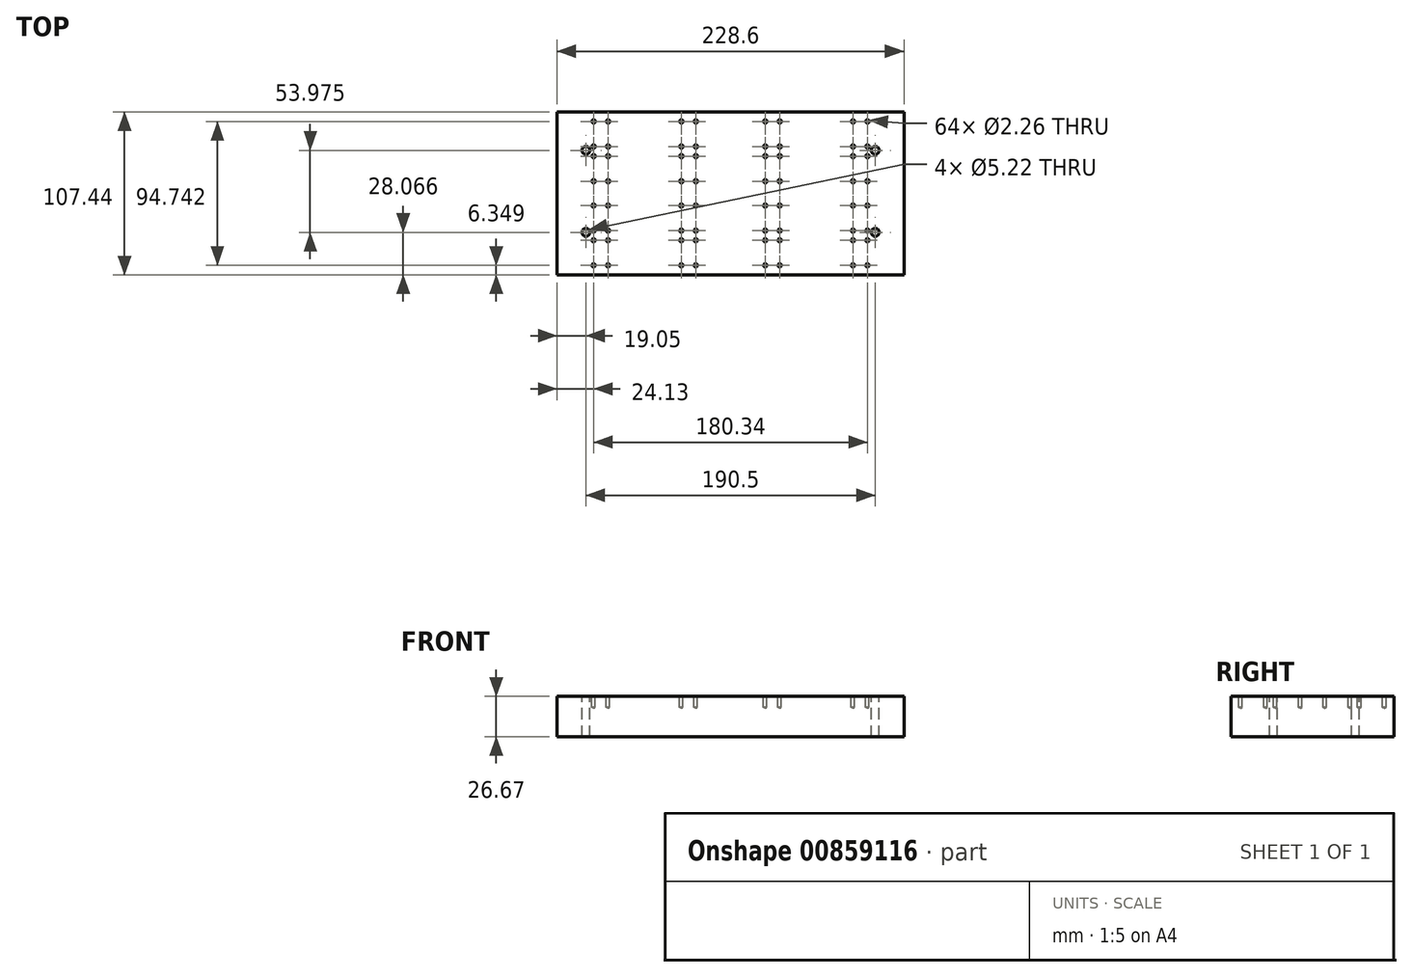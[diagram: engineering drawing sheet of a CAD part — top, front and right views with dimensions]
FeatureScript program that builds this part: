
annotation { "Feature Type Name" : "Feature", "Feature Type Description" : "" }
export const myFeature = defineFeature(function(context is Context, id is Id, definition is map)
    precondition{}
    {
        {
            var Q0;
            Q0=qCreatedBy(makeId("Top.planeOp"),FACE);
            var sketch = newSketch(context, id + "F0", { "sketchPlane" : qUnion([Q0])});
            skLineSegment(sketch, "E0.bottom", {"start": v(-114.3, 53.72) * mm, "end": v(114.3, 53.72) * mm});
            skLineSegment(sketch, "E0.top", {"start": v(-114.3, -53.72) * mm, "end": v(114.3, -53.72) * mm});
            skLineSegment(sketch, "E0.left", {"start": v(-114.3, 53.72) * mm, "end": v(-114.3, -53.72) * mm});
            skLineSegment(sketch, "E0.right", {"start": v(114.3, 53.72) * mm, "end": v(114.3, -53.72) * mm});
            skPoint(sketch, "E0.middle", {"position": v(0, 0) * mm});
            skSolve(sketch);
        }
        {
            var Q0;
            Q0=makeQuery(id+"F0.imprint","IMPRINT",FACE,{"disambiguationData":[TD([[makeQuery(id+"F0.imprint","IMPRINT",EDGE,{"derivedFrom":sQuery(id+"F0.wireOp",EDGE,"E0.bottom")}),-1.0]])]});
            extrude(context, id + "F1", {"entities" : qUnion([Q0]), "depth" : 26.67 * mm, "offsetDistance" : 25.4 * mm});
        }
        {
            var Q0;
            Q0=makeQuery(id+"F1.opExtrude","CAP_FACE",FACE,{"disambiguationData":[OSD([sQuery(id+"F0.wireOp",EDGE,"E0.bottom"),sQuery(id+"F0.wireOp",EDGE,"E0.top"),sQuery(id+"F0.wireOp",EDGE,"E0.left"),sQuery(id+"F0.wireOp",EDGE,"E0.right")])],"isStart":false});
            var sketch = newSketch(context, id + "F2", { "sketchPlane" : qUnion([Q0])});
            skPoint(sketch, "E1", {"position": v(-95.25, 28.32) * mm});
            skLineSegment(sketch, "E2.0.0", {"start": v(-114.3, 53.72) * mm, "end": v(-114.3, -53.72) * mm});
            skLineSegment(sketch, "E2.0.1", {"start": v(-114.3, -53.72) * mm, "end": v(114.3, -53.72) * mm});
            skLineSegment(sketch, "E2.0.2", {"start": v(114.3, -53.72) * mm, "end": v(114.3, 53.72) * mm});
            skLineSegment(sketch, "E2.0.3", {"start": v(114.3, 53.72) * mm, "end": v(-114.3, 53.72) * mm});
            skLineSegment(sketch, "E3", {"start": v(-114.3, 0) * mm, "end": v(114.3, 0) * mm, "construction": true});
            skLineSegment(sketch, "E4", {"start": v(0, 53.72) * mm, "end": v(0, -53.72) * mm, "construction": true});
            skPoint(sketch, "E5.MirrorP", {"position": v(95.25, 28.32) * mm});
            skPoint(sketch, "E6", {"position": v(-95.25, -25.65) * mm});
            skPoint(sketch, "E7", {"position": v(95.25, -25.65) * mm});
            skSolve(sketch);
        }
        {
            var Q0;
            Q0=sQuery(id+"F2.wireOp",VERTEX,"E1");
            var Q1;
            Q1=sQuery(id+"F2.wireOp",VERTEX,"E6");
            var Q2;
            Q2=sQuery(id+"F2.wireOp",VERTEX,"E5.MirrorP");
            var Q3;
            Q3=sQuery(id+"F2.wireOp",VERTEX,"E7");
            var Q4;
            Q4=makeQuery(id+"F1.opExtrude","SWEPT_BODY",BODY,{"disambiguationData":[OSD([sQuery(id+"F0.wireOp",EDGE,"E0.bottom"),sQuery(id+"F0.wireOp",EDGE,"E0.top"),sQuery(id+"F0.wireOp",EDGE,"E0.left"),sQuery(id+"F0.wireOp",EDGE,"E0.right")])]});
            hole(context, id + "F3", {"style" : HoleStyle.SIMPLE, "endStyle" : HoleEndStyle.THROUGH, "holeDiameter" : 5.22 * mm, "majorDiameter" : 6.35 * mm, "isTappedThrough" : true, "tappedDepth" : 12.7 * mm, "tapClearance" : 3, "locations" : qUnion([Q0, Q1, Q2, Q3]), "scope" : qUnion([Q4])});
        }
        {
            var Q0;
            Q0=makeQuery(id+"F2.imprint","IMPRINT",FACE,{"disambiguationData":[TD([[makeQuery(id+"F2.imprint","IMPRINT",EDGE,{"derivedFrom":sQuery(id+"F2.wireOp",EDGE,"E2.0.0")}),1.0]])]});
            var sketch = newSketch(context, id + "F4", { "sketchPlane" : qUnion([Q0])});
            skLineSegment(sketch, "E8.0", {"start": v(-114.3, 53.72) * mm, "end": v(-114.3, -53.72) * mm});
            skLineSegment(sketch, "E9.0", {"start": v(114.3, 53.72) * mm, "end": v(-114.3, 53.72) * mm});
            skPoint(sketch, "E10.MirrorP", {"position": v(-22.86, 47.37) * mm});
            skPoint(sketch, "E11.MirrorP", {"position": v(-32.39, 47.37) * mm});
            skPoint(sketch, "E12.MirrorP", {"position": v(-32.39, 30.86) * mm});
            skPoint(sketch, "E13.MirrorP", {"position": v(-22.86, 30.86) * mm});
            skPoint(sketch, "E14.MirrorP", {"position": v(-32.38, 8) * mm});
            skPoint(sketch, "E15.MirrorP", {"position": v(-22.86, 8) * mm});
            skPoint(sketch, "E16.MirrorP", {"position": v(-22.86, 24.51) * mm});
            skPoint(sketch, "E17.MirrorP", {"position": v(-32.39, 24.51) * mm});
            skPoint(sketch, "E18.MirrorP", {"position": v(-80.65, 8) * mm});
            skPoint(sketch, "E19.MirrorP", {"position": v(-90.17, 8) * mm});
            skPoint(sketch, "E20.MirrorP", {"position": v(-90.17, 24.51) * mm});
            skPoint(sketch, "E21.MirrorP", {"position": v(-80.65, 24.51) * mm});
            skCircle(sketch, "E22.cCircle", {"center": v(-139.45, 89.42) * mm, "radius": 9.94 * mm, "construction": true});
            skLineSegment(sketch, "E22.0", {"start": v(-150.93, 89.42) * mm, "end": v(-145.2, 99.37) * mm});
            skLineSegment(sketch, "E22.1", {"start": v(-145.2, 99.37) * mm, "end": v(-133.7, 99.37) * mm});
            skLineSegment(sketch, "E22.2", {"start": v(-133.7, 99.37) * mm, "end": v(-127.97, 89.42) * mm});
            skLineSegment(sketch, "E22.3", {"start": v(-127.97, 89.42) * mm, "end": v(-133.7, 79.48) * mm});
            skLineSegment(sketch, "E22.4", {"start": v(-133.7, 79.48) * mm, "end": v(-145.2, 79.48) * mm});
            skLineSegment(sketch, "E22.5", {"start": v(-145.2, 79.48) * mm, "end": v(-150.93, 89.42) * mm});
            skPoint(sketch, "E22.0.midPoint", {"position": v(-148.06, 94.4) * mm});
            skPoint(sketch, "E23", {"position": v(-130.84, 84.45) * mm});
            skLineSegment(sketch, "E24", {"start": v(-133.7, 79.48) * mm, "end": v(-145.2, 99.37) * mm});
            skLineSegment(sketch, "E25", {"start": v(-133.7, 99.37) * mm, "end": v(-145.2, 79.48) * mm});
            skPoint(sketch, "E26", {"position": v(-144.21, 97.67) * mm});
            skPoint(sketch, "E27", {"position": v(-134.69, 97.67) * mm});
            skPoint(sketch, "E28", {"position": v(-134.69, 81.17) * mm});
            skPoint(sketch, "E29", {"position": v(-144.21, 81.17) * mm});
            skLineSegment(sketch, "E30.bottom", {"start": v(-144.21, 81.17) * mm, "end": v(-134.69, 81.17) * mm});
            skLineSegment(sketch, "E30.top", {"start": v(-144.21, 97.67) * mm, "end": v(-134.69, 97.67) * mm});
            skLineSegment(sketch, "E30.left", {"start": v(-144.21, 81.17) * mm, "end": v(-144.21, 97.67) * mm});
            skLineSegment(sketch, "E30.right", {"start": v(-134.69, 81.17) * mm, "end": v(-134.69, 97.67) * mm});
            skPoint(sketch, "E31", {"position": v(-90.17, 47.37) * mm});
            skPoint(sketch, "E32", {"position": v(-80.65, 47.37) * mm});
            skPoint(sketch, "E33", {"position": v(-80.65, 30.86) * mm});
            skPoint(sketch, "E34", {"position": v(-90.17, 30.86) * mm});
            skPoint(sketch, "E35.MirrorP", {"position": v(-32.39, -47.37) * mm});
            skPoint(sketch, "E36.MirrorP", {"position": v(-22.86, -47.37) * mm});
            skPoint(sketch, "E37.MirrorP", {"position": v(-22.86, -30.86) * mm});
            skPoint(sketch, "E38.MirrorP", {"position": v(-32.39, -30.86) * mm});
            skPoint(sketch, "E39.MirrorP", {"position": v(-32.39, -24.51) * mm});
            skPoint(sketch, "E40.MirrorP", {"position": v(-22.86, -24.51) * mm});
            skPoint(sketch, "E41.MirrorP", {"position": v(-22.86, -8) * mm});
            skPoint(sketch, "E42.MirrorP", {"position": v(-32.38, -8) * mm});
            skPoint(sketch, "E43.MirrorP", {"position": v(-80.65, -8) * mm});
            skPoint(sketch, "E44.MirrorP", {"position": v(-90.17, -8) * mm});
            skPoint(sketch, "E45.MirrorP", {"position": v(-80.65, -24.51) * mm});
            skPoint(sketch, "E46.MirrorP", {"position": v(-90.17, -24.51) * mm});
            skPoint(sketch, "E47.MirrorP", {"position": v(-80.65, -30.86) * mm});
            skPoint(sketch, "E48.MirrorP", {"position": v(-80.65, -47.37) * mm});
            skPoint(sketch, "E49.MirrorP", {"position": v(-90.17, -30.86) * mm});
            skPoint(sketch, "E50.MirrorP", {"position": v(-90.17, -47.37) * mm});
            skPoint(sketch, "E51.MirrorP", {"position": v(22.86, 47.37) * mm});
            skPoint(sketch, "E52.MirrorP", {"position": v(32.38, 47.37) * mm});
            skPoint(sketch, "E53.MirrorP", {"position": v(22.86, 30.86) * mm});
            skPoint(sketch, "E54.MirrorP", {"position": v(32.38, 30.86) * mm});
            skPoint(sketch, "E55.MirrorP", {"position": v(22.86, 24.51) * mm});
            skPoint(sketch, "E56.MirrorP", {"position": v(32.38, 24.51) * mm});
            skPoint(sketch, "E57.MirrorP", {"position": v(22.86, 8) * mm});
            skPoint(sketch, "E58.MirrorP", {"position": v(32.38, 8) * mm});
            skPoint(sketch, "E59.MirrorP", {"position": v(22.86, -8) * mm});
            skPoint(sketch, "E60.MirrorP", {"position": v(32.38, -8) * mm});
            skPoint(sketch, "E61.MirrorP", {"position": v(22.86, -24.51) * mm});
            skPoint(sketch, "E62.MirrorP", {"position": v(32.38, -24.51) * mm});
            skPoint(sketch, "E63.MirrorP", {"position": v(22.86, -30.86) * mm});
            skPoint(sketch, "E64.MirrorP", {"position": v(32.38, -30.86) * mm});
            skPoint(sketch, "E65.MirrorP", {"position": v(22.86, -47.37) * mm});
            skPoint(sketch, "E66.MirrorP", {"position": v(32.38, -47.37) * mm});
            skPoint(sketch, "E67.MirrorP", {"position": v(80.65, -47.37) * mm});
            skPoint(sketch, "E68.MirrorP", {"position": v(90.17, -47.37) * mm});
            skPoint(sketch, "E69.MirrorP", {"position": v(80.65, -30.86) * mm});
            skPoint(sketch, "E70.MirrorP", {"position": v(90.17, -30.86) * mm});
            skPoint(sketch, "E71.MirrorP", {"position": v(80.65, -24.51) * mm});
            skPoint(sketch, "E72.MirrorP", {"position": v(90.17, -24.51) * mm});
            skPoint(sketch, "E73.MirrorP", {"position": v(80.65, -8) * mm});
            skPoint(sketch, "E74.MirrorP", {"position": v(90.17, -8) * mm});
            skPoint(sketch, "E75.MirrorP", {"position": v(80.65, 8) * mm});
            skPoint(sketch, "E76.MirrorP", {"position": v(90.17, 8) * mm});
            skPoint(sketch, "E77.MirrorP", {"position": v(80.65, 24.51) * mm});
            skPoint(sketch, "E78.MirrorP", {"position": v(90.17, 24.51) * mm});
            skPoint(sketch, "E79.MirrorP", {"position": v(80.65, 30.86) * mm});
            skPoint(sketch, "E80.MirrorP", {"position": v(90.17, 30.86) * mm});
            skPoint(sketch, "E81.MirrorP", {"position": v(80.65, 47.37) * mm});
            skPoint(sketch, "E82.MirrorP", {"position": v(90.17, 47.37) * mm});
            skSolve(sketch);
        }
        {
            var Q0;
            Q0=sQuery(id+"F4.wireOp",VERTEX,"E31");
            var Q1;
            Q1=sQuery(id+"F4.wireOp",VERTEX,"E32");
            var Q2;
            Q2=sQuery(id+"F4.wireOp",VERTEX,"E33");
            var Q3;
            Q3=sQuery(id+"F4.wireOp",VERTEX,"E34");
            var Q4;
            Q4=sQuery(id+"F4.wireOp",VERTEX,"E20.MirrorP");
            var Q5;
            Q5=sQuery(id+"F4.wireOp",VERTEX,"E21.MirrorP");
            var Q6;
            Q6=sQuery(id+"F4.wireOp",VERTEX,"E18.MirrorP");
            var Q7;
            Q7=sQuery(id+"F4.wireOp",VERTEX,"E19.MirrorP");
            var Q8;
            Q8=sQuery(id+"F4.wireOp",VERTEX,"E44.MirrorP");
            var Q9;
            Q9=sQuery(id+"F4.wireOp",VERTEX,"E43.MirrorP");
            var Q10;
            Q10=sQuery(id+"F4.wireOp",VERTEX,"E45.MirrorP");
            var Q11;
            Q11=sQuery(id+"F4.wireOp",VERTEX,"E46.MirrorP");
            var Q12;
            Q12=sQuery(id+"F4.wireOp",VERTEX,"E49.MirrorP");
            var Q13;
            Q13=sQuery(id+"F4.wireOp",VERTEX,"E47.MirrorP");
            var Q14;
            Q14=sQuery(id+"F4.wireOp",VERTEX,"E48.MirrorP");
            var Q15;
            Q15=sQuery(id+"F4.wireOp",VERTEX,"E50.MirrorP");
            var Q16;
            Q16=sQuery(id+"F4.wireOp",VERTEX,"E11.MirrorP");
            var Q17;
            Q17=sQuery(id+"F4.wireOp",VERTEX,"E10.MirrorP");
            var Q18;
            Q18=sQuery(id+"F4.wireOp",VERTEX,"E13.MirrorP");
            var Q19;
            Q19=sQuery(id+"F4.wireOp",VERTEX,"E12.MirrorP");
            var Q20;
            Q20=sQuery(id+"F4.wireOp",VERTEX,"E17.MirrorP");
            var Q21;
            Q21=sQuery(id+"F4.wireOp",VERTEX,"E16.MirrorP");
            var Q22;
            Q22=sQuery(id+"F4.wireOp",VERTEX,"E15.MirrorP");
            var Q23;
            Q23=sQuery(id+"F4.wireOp",VERTEX,"E14.MirrorP");
            var Q24;
            Q24=sQuery(id+"F4.wireOp",VERTEX,"E42.MirrorP");
            var Q25;
            Q25=sQuery(id+"F4.wireOp",VERTEX,"E41.MirrorP");
            var Q26;
            Q26=sQuery(id+"F4.wireOp",VERTEX,"E40.MirrorP");
            var Q27;
            Q27=sQuery(id+"F4.wireOp",VERTEX,"E39.MirrorP");
            var Q28;
            Q28=sQuery(id+"F4.wireOp",VERTEX,"E38.MirrorP");
            var Q29;
            Q29=sQuery(id+"F4.wireOp",VERTEX,"E37.MirrorP");
            var Q30;
            Q30=sQuery(id+"F4.wireOp",VERTEX,"E36.MirrorP");
            var Q31;
            Q31=sQuery(id+"F4.wireOp",VERTEX,"E35.MirrorP");
            var Q32;
            Q32=sQuery(id+"F4.wireOp",VERTEX,"E51.MirrorP");
            var Q33;
            Q33=sQuery(id+"F4.wireOp",VERTEX,"E52.MirrorP");
            var Q34;
            Q34=sQuery(id+"F4.wireOp",VERTEX,"E54.MirrorP");
            var Q35;
            Q35=sQuery(id+"F4.wireOp",VERTEX,"E53.MirrorP");
            var Q36;
            Q36=sQuery(id+"F4.wireOp",VERTEX,"E55.MirrorP");
            var Q37;
            Q37=sQuery(id+"F4.wireOp",VERTEX,"E56.MirrorP");
            var Q38;
            Q38=sQuery(id+"F4.wireOp",VERTEX,"E58.MirrorP");
            var Q39;
            Q39=sQuery(id+"F4.wireOp",VERTEX,"E57.MirrorP");
            var Q40;
            Q40=sQuery(id+"F4.wireOp",VERTEX,"E59.MirrorP");
            var Q41;
            Q41=sQuery(id+"F4.wireOp",VERTEX,"E60.MirrorP");
            var Q42;
            Q42=sQuery(id+"F4.wireOp",VERTEX,"E62.MirrorP");
            var Q43;
            Q43=sQuery(id+"F4.wireOp",VERTEX,"E61.MirrorP");
            var Q44;
            Q44=sQuery(id+"F4.wireOp",VERTEX,"E63.MirrorP");
            var Q45;
            Q45=sQuery(id+"F4.wireOp",VERTEX,"E64.MirrorP");
            var Q46;
            Q46=sQuery(id+"F4.wireOp",VERTEX,"E66.MirrorP");
            var Q47;
            Q47=sQuery(id+"F4.wireOp",VERTEX,"E65.MirrorP");
            var Q48;
            Q48=sQuery(id+"F4.wireOp",VERTEX,"E82.MirrorP");
            var Q49;
            Q49=sQuery(id+"F4.wireOp",VERTEX,"E81.MirrorP");
            var Q50;
            Q50=sQuery(id+"F4.wireOp",VERTEX,"E79.MirrorP");
            var Q51;
            Q51=sQuery(id+"F4.wireOp",VERTEX,"E80.MirrorP");
            var Q52;
            Q52=sQuery(id+"F4.wireOp",VERTEX,"E78.MirrorP");
            var Q53;
            Q53=sQuery(id+"F4.wireOp",VERTEX,"E77.MirrorP");
            var Q54;
            Q54=sQuery(id+"F4.wireOp",VERTEX,"E75.MirrorP");
            var Q55;
            Q55=sQuery(id+"F4.wireOp",VERTEX,"E76.MirrorP");
            var Q56;
            Q56=sQuery(id+"F4.wireOp",VERTEX,"E74.MirrorP");
            var Q57;
            Q57=sQuery(id+"F4.wireOp",VERTEX,"E73.MirrorP");
            var Q58;
            Q58=sQuery(id+"F4.wireOp",VERTEX,"E71.MirrorP");
            var Q59;
            Q59=sQuery(id+"F4.wireOp",VERTEX,"E72.MirrorP");
            var Q60;
            Q60=sQuery(id+"F4.wireOp",VERTEX,"E70.MirrorP");
            var Q61;
            Q61=sQuery(id+"F4.wireOp",VERTEX,"E69.MirrorP");
            var Q62;
            Q62=sQuery(id+"F4.wireOp",VERTEX,"E67.MirrorP");
            var Q63;
            Q63=sQuery(id+"F4.wireOp",VERTEX,"E68.MirrorP");
            var Q64;
            Q64=makeQuery(id+"F1.opExtrude","SWEPT_BODY",BODY,{"disambiguationData":[OSD([sQuery(id+"F0.wireOp",EDGE,"E0.bottom"),sQuery(id+"F0.wireOp",EDGE,"E0.top"),sQuery(id+"F0.wireOp",EDGE,"E0.left"),sQuery(id+"F0.wireOp",EDGE,"E0.right")])]});
            hole(context, id + "F5", {"style" : HoleStyle.SIMPLE, "endStyle" : HoleEndStyle.BLIND, "standardTappedOrClearance" : lookupTablePath({ "standard" : "ANSI", "engagement" : "75%", "pitch" : "40 tpi", "size" : "#4", "type" : "Tapped" }), "standardBlindInLast" : lookupTablePath({ "standard" : "ANSI", "engagement" : "75%", "pitch" : "40 tpi", "size" : "#4", "type" : "Tapped" }), "holeDiameter" : 2.26 * mm, "majorDiameter" : 2.84 * mm, "showTappedDepth" : true, "holeDepth" : 7.11 * mm, "isTappedThrough" : true, "tappedDepth" : 5.2 * mm, "tapClearance" : 3, "locations" : qUnion([Q0, Q1, Q2, Q3, Q4, Q5, Q6, Q7, Q8, Q9, Q10, Q11, Q12, Q13, Q14, Q15, Q16, Q17, Q18, Q19, Q20, Q21, Q22, Q23, Q24, Q25, Q26, Q27, Q28, Q29, Q30, Q31, Q32, Q33, Q34, Q35, Q36, Q37, Q38, Q39, Q40, Q41, Q42, Q43, Q44, Q45, Q46, Q47, Q48, Q49, Q50, Q51, Q52, Q53, Q54, Q55, Q56, Q57, Q58, Q59, Q60, Q61, Q62, Q63]), "scope" : qUnion([Q64])});
        }
    });
